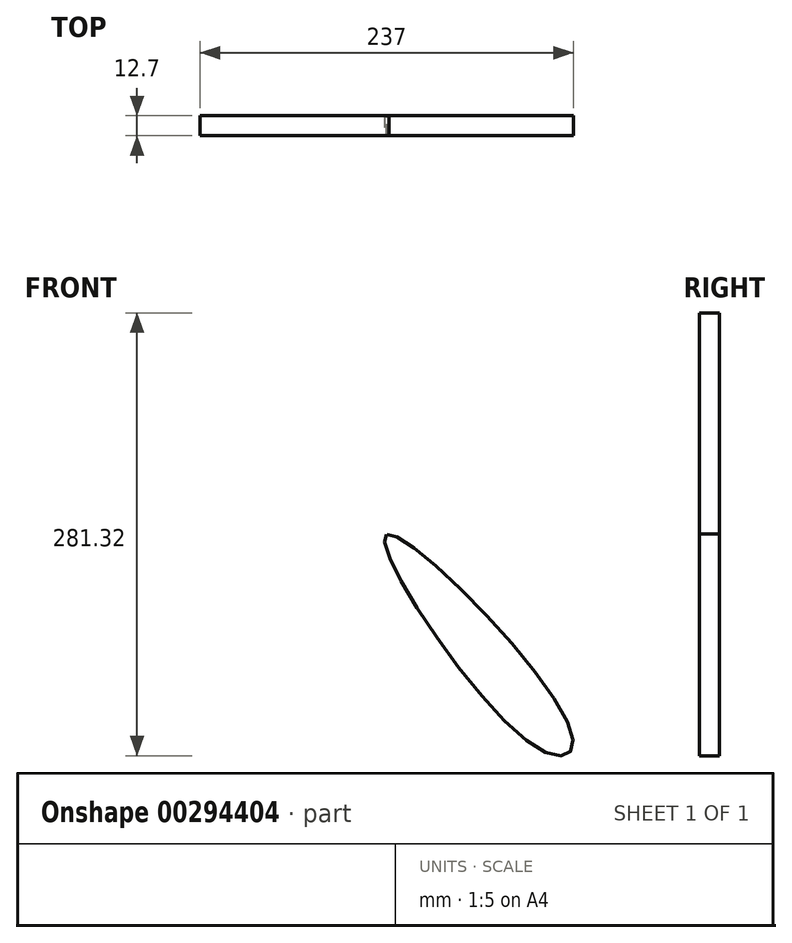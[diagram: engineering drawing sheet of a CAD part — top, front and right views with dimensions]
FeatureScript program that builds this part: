
annotation { "Feature Type Name" : "Feature", "Feature Type Description" : "" }
export const myFeature = defineFeature(function(context is Context, id is Id, definition is map)
    precondition{}
    {
        {
            var Q0;
            Q0=qCreatedBy(makeId("Front.planeOp"),FACE);
            var sketch = newSketch(context, id + "F0", { "sketchPlane" : qUnion([Q0])});
            skPoint(sketch, "E0", {"position": v(0.09, 0.04) * mm});
            skFitSpline(sketch, "E1", {"points": [v(0.09, 0.04) * mm, v(-118.16, 128.56) * mm, v(-96.74, 136.27) * mm, v(0.09, 0.04) * mm]});
            skFitSpline(sketch, "E2", {"points": [v(-0.12, -0.05) * mm, v(118.12, -128.58) * mm, v(96.7, -136.29) * mm, v(-0.12, -0.05) * mm]});
            skSolve(sketch);
        }
        {
            var Q0;
            Q0=qSketchRegion(id+"F0",true);
            extrude(context, id + "F1", {"entities" : qUnion([Q0]), "depth" : 12.7 * mm, "offsetDistance" : 25.4 * mm});
        }
    });
